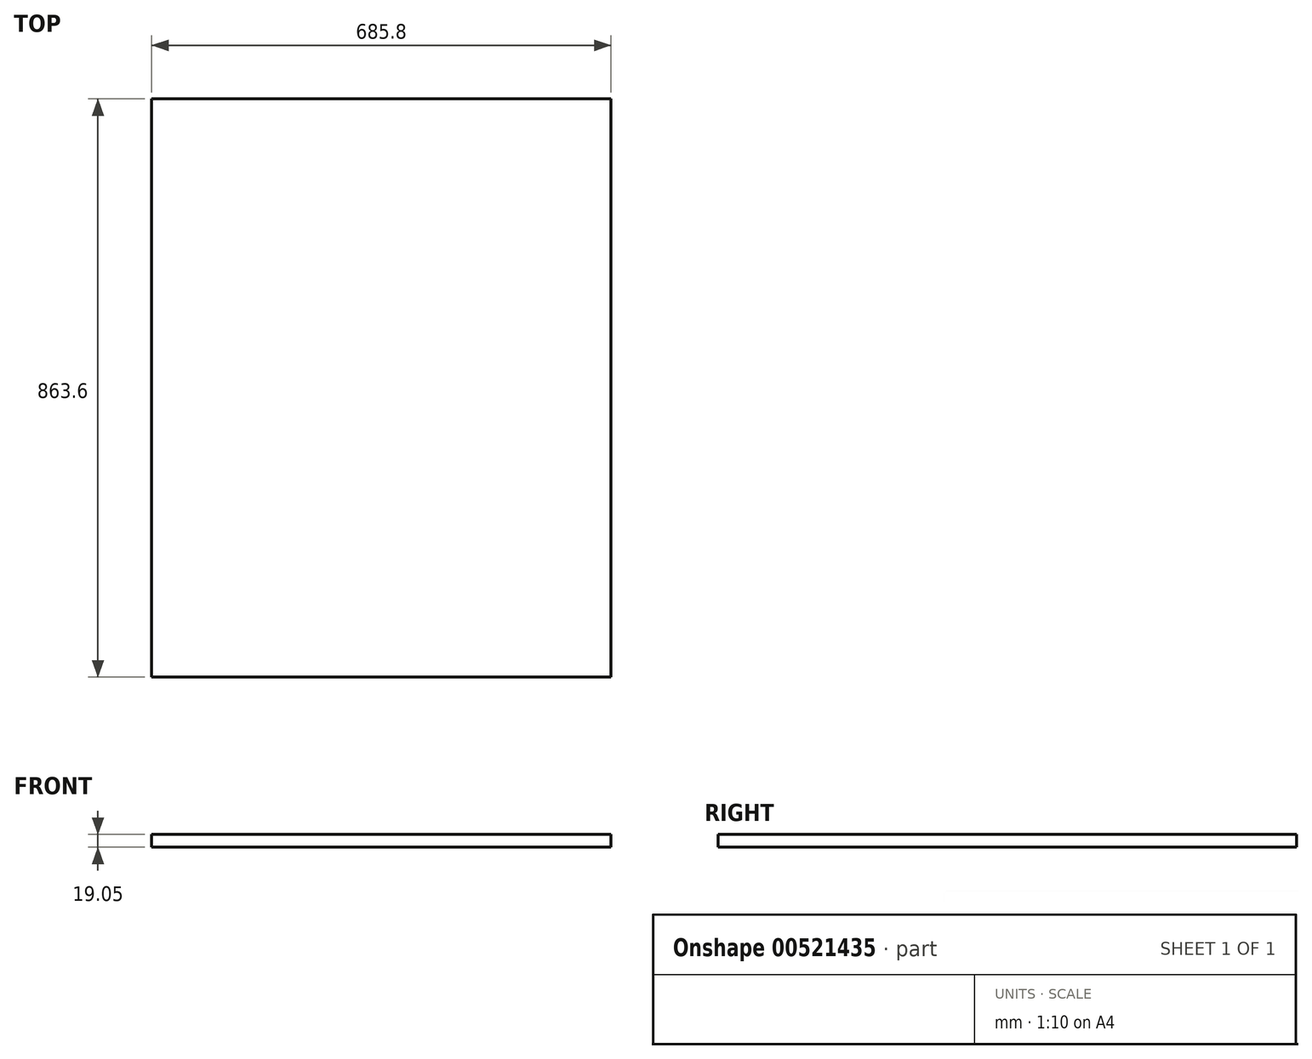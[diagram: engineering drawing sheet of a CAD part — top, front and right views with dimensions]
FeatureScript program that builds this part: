
annotation { "Feature Type Name" : "Feature", "Feature Type Description" : "" }
export const myFeature = defineFeature(function(context is Context, id is Id, definition is map)
    precondition{}
    {
        {
            var Q0;
            Q0=qCreatedBy(makeId("Top.planeOp"),FACE);
            var sketch = newSketch(context, id + "F0", { "sketchPlane" : qUnion([Q0])});
            skLineSegment(sketch, "E0.bottom", {"start": v(-340.75, 462.28) * mm, "end": v(345.05, 462.28) * mm});
            skLineSegment(sketch, "E0.top", {"start": v(-340.75, -401.32) * mm, "end": v(345.05, -401.32) * mm});
            skLineSegment(sketch, "E0.left", {"start": v(-340.75, 462.28) * mm, "end": v(-340.75, -401.32) * mm});
            skLineSegment(sketch, "E0.right", {"start": v(345.05, 462.28) * mm, "end": v(345.05, -401.32) * mm});
            skSolve(sketch);
        }
        {
            var Q0;
            Q0=makeQuery(id+"F0.imprint","IMPRINT",FACE,{"disambiguationData":[TD([[makeQuery(id+"F0.imprint","IMPRINT",EDGE,{"derivedFrom":sQuery(id+"F0.wireOp",EDGE,"E0.bottom")}),-1.0]])]});
            extrude(context, id + "F1", {"entities" : qUnion([Q0]), "depth" : 19.05 * mm, "offsetDistance" : 25.4 * mm});
        }
    });
